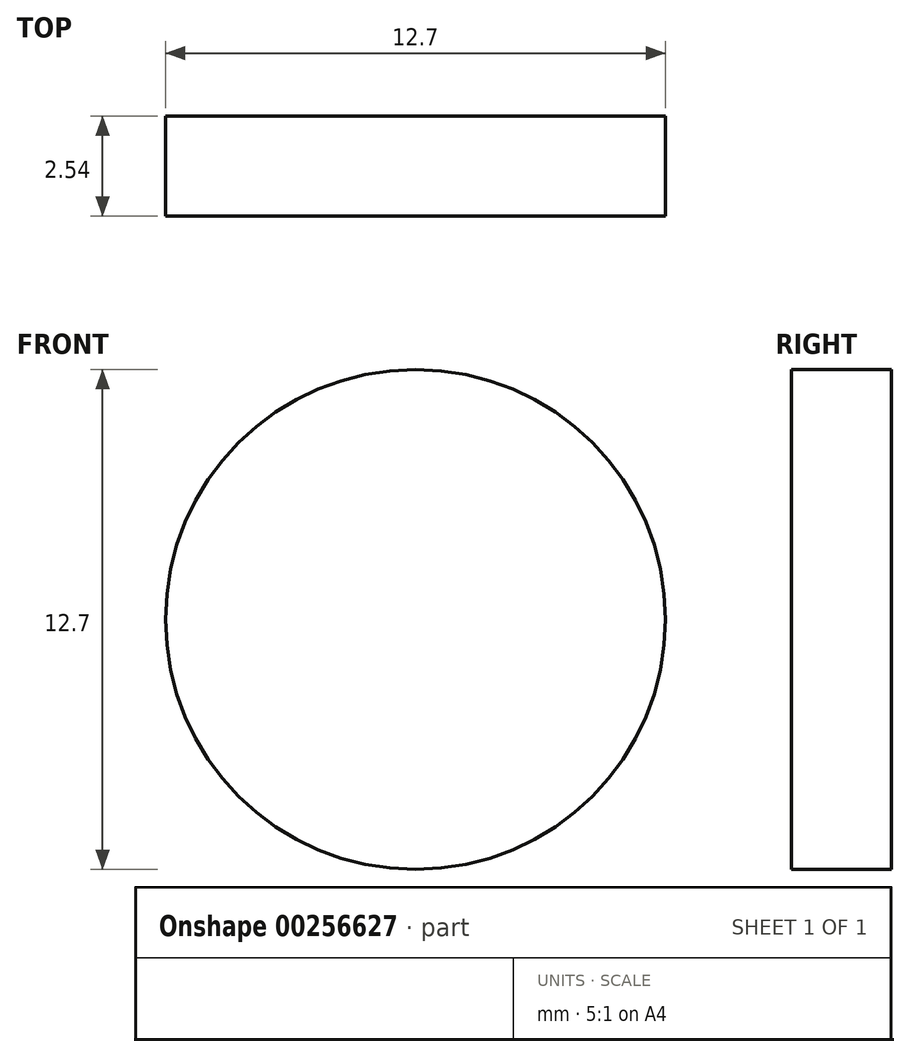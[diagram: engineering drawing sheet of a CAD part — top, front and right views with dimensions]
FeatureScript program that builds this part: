
annotation { "Feature Type Name" : "Feature", "Feature Type Description" : "" }
export const myFeature = defineFeature(function(context is Context, id is Id, definition is map)
    precondition{}
    {
        {
            var Q0;
            Q0=qCreatedBy(makeId("Front.planeOp"),FACE);
            var sketch = newSketch(context, id + "F0", { "sketchPlane" : qUnion([Q0])});
            skCircle(sketch, "E0", {"center": v(0, 0) * mm, "radius": 6.35 * mm});
            skSolve(sketch);
        }
        {
            var Q0;
            Q0=makeQuery(id+"F0.imprint","IMPRINT",FACE,{"disambiguationData":[TD([[makeQuery(id+"F0.imprint","IMPRINT",EDGE,{"derivedFrom":sQuery(id+"F0.wireOp",EDGE,"E0")}),1.0]])]});
            extrude(context, id + "F1", {"entities" : qUnion([Q0]), "depth" : 2.54 * mm});
        }
    });
